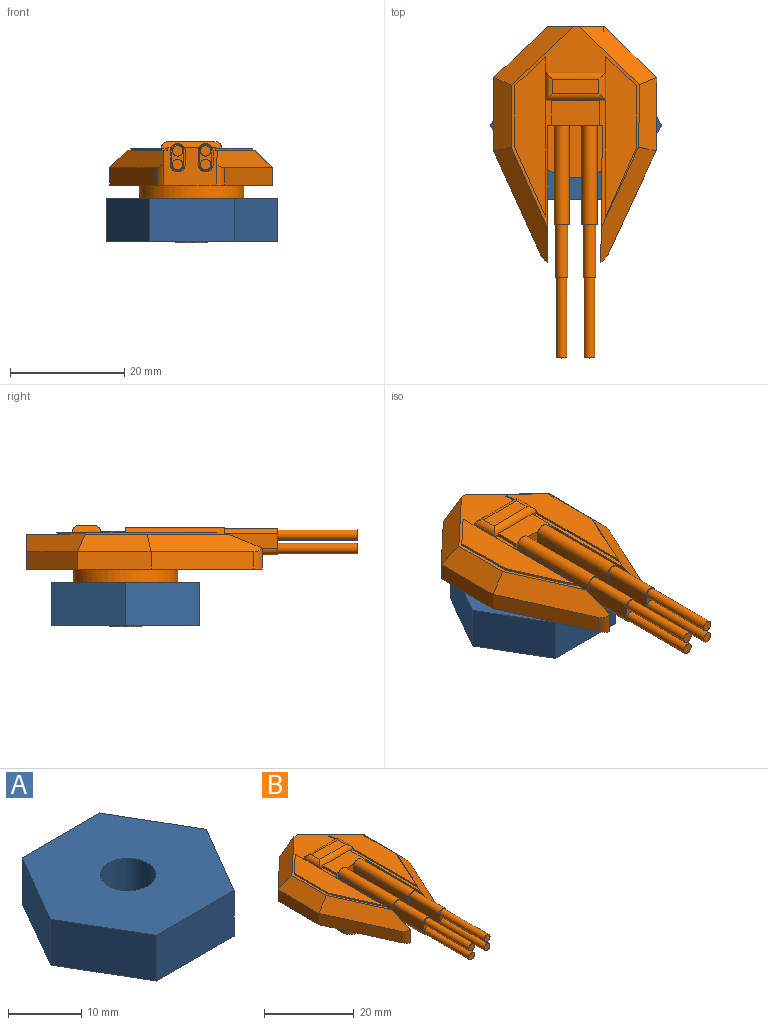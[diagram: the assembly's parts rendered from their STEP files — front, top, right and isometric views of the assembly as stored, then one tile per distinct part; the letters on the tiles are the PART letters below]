
ASSEMBLY  parts=2 mates=1
PART A: 9 faces, bbox 30x25.9x7.6 mm
  f0: plane 14.94x7.62mm, normal (0,1,0), area 113.8mm2, adj f1,f5,f6,f7
  f1: plane 13.03x7.62mm, normal (-0.87,0.5,0), area 114.6mm2, adj f0,f2,f6,f7
  f2: plane 12.88x7.62mm, normal (-0.86,-0.5,0), area 113.7mm2, adj f1,f3,f6,f7
  f3: plane 14.93x7.62mm, normal (0,-1,0), area 113.8mm2, adj f2,f4,f6,f7
  f4: plane 12.88x7.62mm, normal (0.86,-0.51,0), area 113.7mm2, adj f3,f5,f6,f7
  f5: plane 13.03x7.62mm, normal (0.87,0.5,0), area 114.7mm2, adj f0,f4,f6,f7
  f6: plane 30x25.91mm, normal (0,0,1), area 536.5mm2, adj f0,f1,f2,f3,f4,f5,f8
  f7: plane 30x25.91mm, normal (0,0,-1), area 536.5mm2, adj f0,f1,f2,f3,f4,f5,f8
  f8: cylinder r=3.81mm len=7.62mm, axis (0,0,1), area 182.4mm2, adj f6,f7
PART B: 82 faces, bbox 28.6x58.1x17.7 mm
  f0: plane 1.1x0.34mm, normal (0,-1,0), area 0.4mm2, adj f1,f3,f69,f72,f76
  f1: plane 35.29x22.44mm, normal (0,0,1), area 120.5mm2, adj f0,f2,f3,f9,f14,f15,f19,f24
  f2: plane 20.29x0.34mm, normal (1,0,0), area 6.8mm2, adj f1,f58,f62,f73
  f3: plane 20.29x0.34mm, normal (-1,0,0), area 6.8mm2, adj f0,f1,f63,f67
  f4: plane 2.23x0.61mm, normal (0,1,0), area 1mm2, adj f31,f70
  f5: plane 2.23x0.61mm, normal (0,1,0), area 1mm2, adj f34,f70
  f6: plane 4.95x2.65mm, normal (0,-1,0), area 2.6mm2, adj f34,f35,f36,f37,f43,f44,f45,f46
  f7: plane 4.95x2.65mm, normal (0,-1,0), area 2.6mm2, adj f30,f31,f32,f33,f38,f39,f40,f41
  f8: plane 9.56x9.14mm, normal (0,0,1), area 82.9mm2, adj f9,f11,f15,f19
  f9: plane 9.56x6.63mm, normal (0,-1,0), area 41.6mm2, adj f1,f8,f15,f19,f30,f31,f32,f33
  f10: plane 3.73x0.8mm, normal (1,0,0), area 2.7mm2, adj f13,f14,f20,f29
  f11: cylinder r=9.14mm len=18.29mm, axis (0,0,-1), area 131.3mm2, adj f8,f12,f13
  f12: plane 18.29x18.29mm, normal (0,0,-1), area 237mm2, adj f11,f80
  f13: plane 41.31x28.56mm, normal (0,0,-1), area 510.5mm2, adj f10,f11,f14,f15,f16,f17,f18,f19
  f14: plane 9.75x6.1mm, normal (0,1,0), area 46.4mm2, adj f1,f10,f13,f16,f24,f29
  f15: plane 23.91x6.1mm, normal (1,0,0), area 138.6mm2, adj f1,f8,f9,f13,f26,f57
  f16: plane 9.45x8.88mm, normal (-0.69,0.73,0), area 39.5mm2, adj f13,f14,f17,f24
  f17: plane 12.86x3.05mm, normal (-1,0,0), area 39.2mm2, adj f13,f16,f18,f25
  f18: plane 18.01x8.12mm, normal (-0.91,-0.41,0), area 60.2mm2, adj f13,f17,f26,f57
  f19: plane 23.91x6.1mm, normal (-1,0.01,0), area 138.3mm2, adj f1,f8,f9,f13,f27,f56
  f20: plane 3.73x0.93mm, normal (-1,0.01,0), area 3.2mm2, adj f10,f13,f23,f29
  f21: plane 18.09x8.41mm, normal (0.91,-0.42,0), area 60.8mm2, adj f13,f22,f27,f56
  f22: plane 12.86x3.05mm, normal (1,-0.01,0), area 39.2mm2, adj f13,f21,f23,f28
  f23: plane 9.34x8.99mm, normal (0.69,0.72,0), area 39.5mm2, adj f13,f20,f22,f29
  f24: plane 13.9x10.2mm, normal (-0.48,0.52,0.71), area 60mm2, adj f1,f14,f16,f25
  f25: plane 12.86x3.05mm, normal (-0.71,0,0.71), area 51.2mm2, adj f1,f17,f24,f26
  f26: plane 20.09x9.45mm, normal (-0.64,-0.29,0.71), area 82mm2, adj f1,f15,f18,f25,f57
  f27: plane 20.15x9.68mm, normal (0.64,-0.3,0.71), area 82.2mm2, adj f1,f19,f21,f28,f56
  f28: plane 12.86x3.19mm, normal (0.71,-0.01,0.71), area 51.2mm2, adj f1,f22,f27,f29
  f29: plane 13.6x10.28mm, normal (0.49,0.51,0.71), area 59.1mm2, adj f1,f10,f14,f20,f23,f28
  f30: plane 17.37x2.19mm, normal (1,0,0), area 38mm2, adj f7,f9,f31,f33
  f31: cylinder r=1.32mm len=17.37mm, axis (0,1,0), area 73.7mm2, adj f4,f7,f9,f30,f32
  f32: plane 17.37x2.04mm, normal (-1,0,0), area 35.4mm2, adj f7,f9,f31,f33
  f33: cylinder r=1.33mm len=17.37mm, axis (0,1,0), area 77.2mm2, adj f7,f9,f30,f32
  f34: cylinder r=1.32mm len=17.37mm, axis (0,1,0), area 73.7mm2, adj f5,f6,f9,f35,f37
  f35: plane 17.37x2.19mm, normal (-1,0,0), area 38mm2, adj f6,f9,f34,f36
  f36: cylinder r=1.33mm len=17.37mm, axis (0,1,0), area 77.2mm2, adj f6,f9,f35,f37
  f37: plane 17.37x2.04mm, normal (1,0,0), area 35.4mm2, adj f6,f9,f34,f36
  f38: plane 9.3x2.59mm, normal (1,0,0), area 24mm2, adj f7,f39,f41,f42
  f39: cylinder r=1.1mm len=9.3mm, axis (0,1,0), area 29.5mm2, adj f7,f38,f40,f42
  f40: plane 9.3x2.48mm, normal (-1,0,0), area 23.1mm2, adj f7,f39,f41,f42
  f41: cylinder r=1.09mm len=9.3mm, axis (0,1,0), area 31.7mm2, adj f7,f38,f40,f42
  f42: plane 4.58x2.18mm, normal (0,-1,0), area 3.7mm2, adj f38,f39,f40,f41,f48,f50
  f43: cylinder r=1.1mm len=9.3mm, axis (0,1,0), area 29.5mm2, adj f6,f44,f46,f47
  f44: plane 9.3x2.59mm, normal (-1,0,0), area 24mm2, adj f6,f43,f45,f47
  f45: cylinder r=1.09mm len=9.3mm, axis (0,1,0), area 31.7mm2, adj f6,f44,f46,f47
  f46: plane 9.3x2.48mm, normal (1,0,0), area 23.1mm2, adj f6,f43,f45,f47
  f47: plane 4.58x2.18mm, normal (0,-1,0), area 3.7mm2, adj f43,f44,f45,f46,f52,f54
  f48: cylinder r=0.91mm len=14.02mm, axis (0,1,0), area 80.6mm2, adj f42,f49
  f49: plane 1.83x1.83mm, normal (0,-1,0), area 2.6mm2, adj f48
  f50: cylinder r=0.91mm len=14.02mm, axis (0,1,0), area 80.6mm2, adj f42,f51
  f51: plane 1.83x1.83mm, normal (0,-1,0), area 2.6mm2, adj f50
  f52: cylinder r=0.91mm len=14.02mm, axis (0,1,0), area 80.6mm2, adj f47,f53
  f53: plane 1.83x1.83mm, normal (0,-1,0), area 2.6mm2, adj f52
  f54: cylinder r=0.91mm len=14.02mm, axis (0,1,0), area 80.6mm2, adj f47,f55
  f55: plane 1.83x1.83mm, normal (0,-1,0), area 2.6mm2, adj f54
  f56: cylinder r=3.05mm len=3.62mm, axis (0,0,1), area 6.1mm2, adj f13,f19,f21,f27
  f57: cylinder r=3.05mm len=3.67mm, axis (0,0,1), area 6.5mm2, adj f13,f15,f18,f26
  f58: plane 12.13x5.39mm, normal (-0.91,-0.41,0), area 4.4mm2, adj f1,f2,f61,f62
  f59: plane 2.71x0.34mm, normal (1,0,0), area 0.9mm2, adj f1,f60,f62,f74
  f60: plane 5.39x5.07mm, normal (-0.69,0.73,0), area 2.5mm2, adj f1,f59,f61,f62
  f61: plane 10.76x0.34mm, normal (-1,0,0), area 3.6mm2, adj f1,f58,f60,f62
  f62: plane 27.95x5.39mm, normal (0,0,1), area 104.3mm2, adj f2,f58,f59,f60,f61,f71
  f63: plane 12.13x5.39mm, normal (0.91,-0.41,0), area 4.4mm2, adj f1,f3,f64,f67
  f64: plane 10.76x0.34mm, normal (1,0,0), area 3.6mm2, adj f1,f63,f65,f67
  f65: plane 5.39x5.07mm, normal (0.69,0.73,0), area 2.5mm2, adj f1,f64,f66,f67
  f66: plane 2.71x0.34mm, normal (-1,0,0), area 0.9mm2, adj f1,f65,f67,f74
  f67: plane 27.95x5.39mm, normal (0,0,1), area 104.2mm2, adj f3,f63,f64,f65,f66,f72
  f68: plane 4.36x0.53mm, normal (-1,0,0), area 2.3mm2, adj f1,f9,f70,f73,f76
  f69: plane 4.36x0.53mm, normal (1,0,0), area 2.3mm2, adj f0,f1,f9,f70,f76
  f70: plane 8.4x4.36mm, normal (0,0,1), area 36.6mm2, adj f4,f5,f9,f68,f69,f76
  f71: plane 4.95x0mm, normal (-1,0,0), area 0mm2, adj f62,f73,f74,f77
  f72: plane 4.95x0mm, normal (1,0,0), area 0mm2, adj f0,f67,f74,f78
  f73: plane 1.03x0.34mm, normal (0,-1,0), area 0.3mm2, adj f1,f2,f68,f71,f76
  f74: plane 10.54x0.34mm, normal (0,1,0), area 3.6mm2, adj f1,f59,f66,f71,f72,f79
  f75: plane 8.17x2.58mm, normal (0,0,1), area 21.1mm2, adj f76,f77,f78,f79
  f76: cylinder r=1.19mm len=10.54mm, axis (-1,0,0), area 16.4mm2, adj f0,f68,f69,f70,f73,f75,f77,f78
  f77: cylinder r=1.19mm len=4.95mm, axis (0,1,0), area 7.6mm2, adj f71,f75,f76,f79
  f78: cylinder r=1.19mm len=4.95mm, axis (0,-1,0), area 7.6mm2, adj f72,f75,f76,f79
  f79: cylinder r=1.19mm len=10.54mm, axis (1,0,0), area 18mm2, adj f74,f75,f77,f78
  f80: cylinder r=2.86mm len=7.77mm, axis (0,0,1), area 139.5mm2, adj f12,f81
  f81: plane 5.72x5.72mm, normal (0,0,-1), area 25.7mm2, adj f80
PLACE A t=(-2.08,-7.35,2.67)mm
PLACE B at identity
MATE fastened A.f8 <-> B.f11  axis (0,0,1) through (2.93,-15.94,3.94)mm
